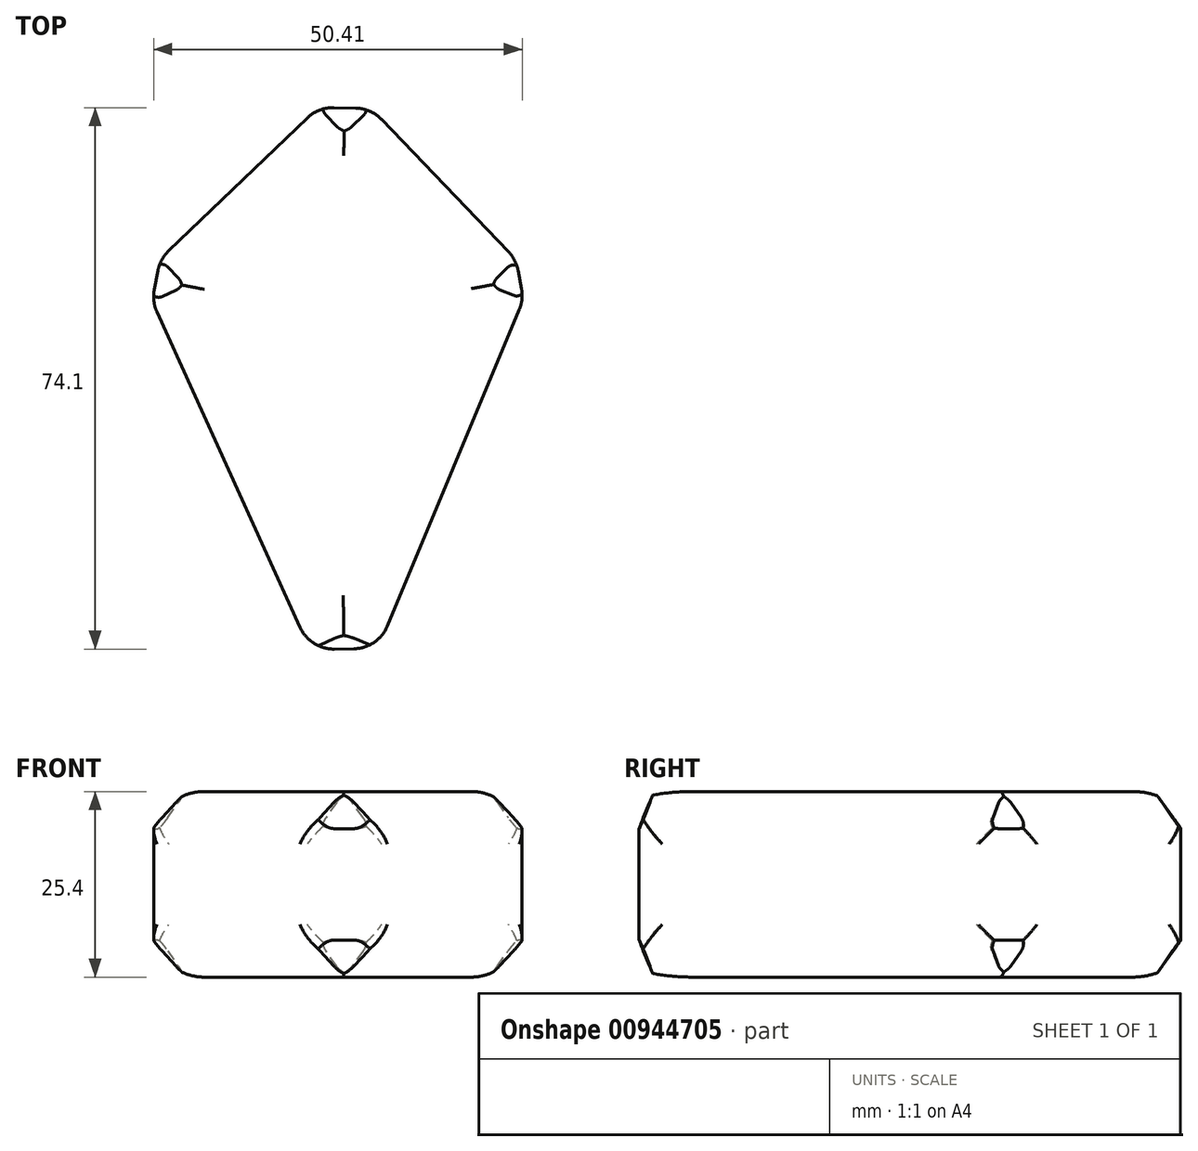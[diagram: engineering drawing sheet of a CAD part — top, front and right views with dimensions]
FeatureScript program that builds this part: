
annotation { "Feature Type Name" : "Feature", "Feature Type Description" : "" }
export const myFeature = defineFeature(function(context is Context, id is Id, definition is map)
    precondition{}
    {
        {
            var Q0;
            Q0=qCreatedBy(makeId("Top.planeOp"),FACE);
            var sketch = newSketch(context, id + "F0", { "sketchPlane" : qUnion([Q0])});
            skLineSegment(sketch, "E0", {"start": v(-39.57, 36.7) * mm, "end": v(-11.66, 63.46) * mm});
            skLineSegment(sketch, "E1", {"start": v(-11.66, 63.46) * mm, "end": v(14, 36.7) * mm});
            skLineSegment(sketch, "E2", {"start": v(14, 36.7) * mm, "end": v(-11.66, -24.9) * mm});
            skLineSegment(sketch, "E3", {"start": v(-11.66, -24.9) * mm, "end": v(-39.57, 36.7) * mm});
            skSolve(sketch);
        }
        {
            var Q0;
            Q0 = qSketchRegion(id + "F0", true);
            extrude(context, id + "F1", {"entities" : qUnion([Q0]), "depth" : 25.4 * mm, "offsetDistance" : 25.4 * mm});
        }
        {
            var Q0;
            Q0=makeQuery(id+"F1.opExtrude","CAP_FACE",FACE,{"disambiguationData":[OSD([sQuery(id+"F0.wireOp",EDGE,"E0"),sQuery(id+"F0.wireOp",EDGE,"E1"),sQuery(id+"F0.wireOp",EDGE,"E2"),sQuery(id+"F0.wireOp",EDGE,"E3")])],"isStart":false});
            var Q1;
            Q1=makeQuery(id+"F1.opExtrude","CAP_FACE",FACE,{"disambiguationData":[OSD([sQuery(id+"F0.wireOp",EDGE,"E0"),sQuery(id+"F0.wireOp",EDGE,"E1"),sQuery(id+"F0.wireOp",EDGE,"E2"),sQuery(id+"F0.wireOp",EDGE,"E3")])],"isStart":true});
            var Q2;
            Q2=makeQuery(id+"F1.opExtrude","SWEPT_EDGE",EDGE,{"disambiguationData":[OSD([sQuery(id+"F0.wireOp",EDGE,"E1"),sQuery(id+"F0.wireOp",EDGE,"E2")])]});
            var Q3;
            Q3=makeQuery(id+"F1.opExtrude","SWEPT_EDGE",EDGE,{"disambiguationData":[OSD([sQuery(id+"F0.wireOp",EDGE,"E2"),sQuery(id+"F0.wireOp",EDGE,"E3")])]});
            var Q4;
            Q4=makeQuery(id+"F1.opExtrude","SWEPT_EDGE",EDGE,{"disambiguationData":[OSD([sQuery(id+"F0.wireOp",EDGE,"E0"),sQuery(id+"F0.wireOp",EDGE,"E3")])]});
            var Q5;
            Q5=makeQuery(id+"F1.opExtrude","SWEPT_EDGE",EDGE,{"disambiguationData":[OSD([sQuery(id+"F0.wireOp",EDGE,"E0"),sQuery(id+"F0.wireOp",EDGE,"E1")])]});
            chamfer(context, id + "F2", {"entities" : qUnion([Q0, Q1, Q2, Q3, Q4, Q5]), "width" : 5.08 * mm, "tangentPropagation" : true});
        }
        {
            var Q0;
            Q0=makeQuery(id+"F1.opExtrude","CAP_FACE",FACE,{"disambiguationData":[OSD([sQuery(id+"F0.wireOp",EDGE,"E0"),sQuery(id+"F0.wireOp",EDGE,"E1"),sQuery(id+"F0.wireOp",EDGE,"E2"),sQuery(id+"F0.wireOp",EDGE,"E3")])],"isStart":false});
            var Q1;
            Q1=makeQuery(id+"F1.opExtrude","CAP_FACE",FACE,{"disambiguationData":[OSD([sQuery(id+"F0.wireOp",EDGE,"E0"),sQuery(id+"F0.wireOp",EDGE,"E1"),sQuery(id+"F0.wireOp",EDGE,"E2"),sQuery(id+"F0.wireOp",EDGE,"E3")])],"isStart":true});
            var Q2;
            Q2=makeQuery(id+"F1.opExtrude","SWEPT_FACE",FACE,{"disambiguationData":[OSD([sQuery(id+"F0.wireOp",EDGE,"E1")])]});
            var Q3;
            Q3=makeQuery(id+"F1.opExtrude","SWEPT_FACE",FACE,{"disambiguationData":[OSD([sQuery(id+"F0.wireOp",EDGE,"E2")])]});
            var Q4;
            Q4=makeQuery(id+"F1.opExtrude","SWEPT_FACE",FACE,{"disambiguationData":[OSD([sQuery(id+"F0.wireOp",EDGE,"E3")])]});
            var Q5;
            Q5=makeQuery(id+"F1.opExtrude","SWEPT_FACE",FACE,{"disambiguationData":[OSD([sQuery(id+"F0.wireOp",EDGE,"E0")])]});
            fillet(context, id + "F3", {"entities" : qUnion([Q0, Q1, Q2, Q3, Q4, Q5]), "radius" : 5.08 * mm, "tangentPropagation" : true, "allowEdgeOverflow" : false});
        }
    });
